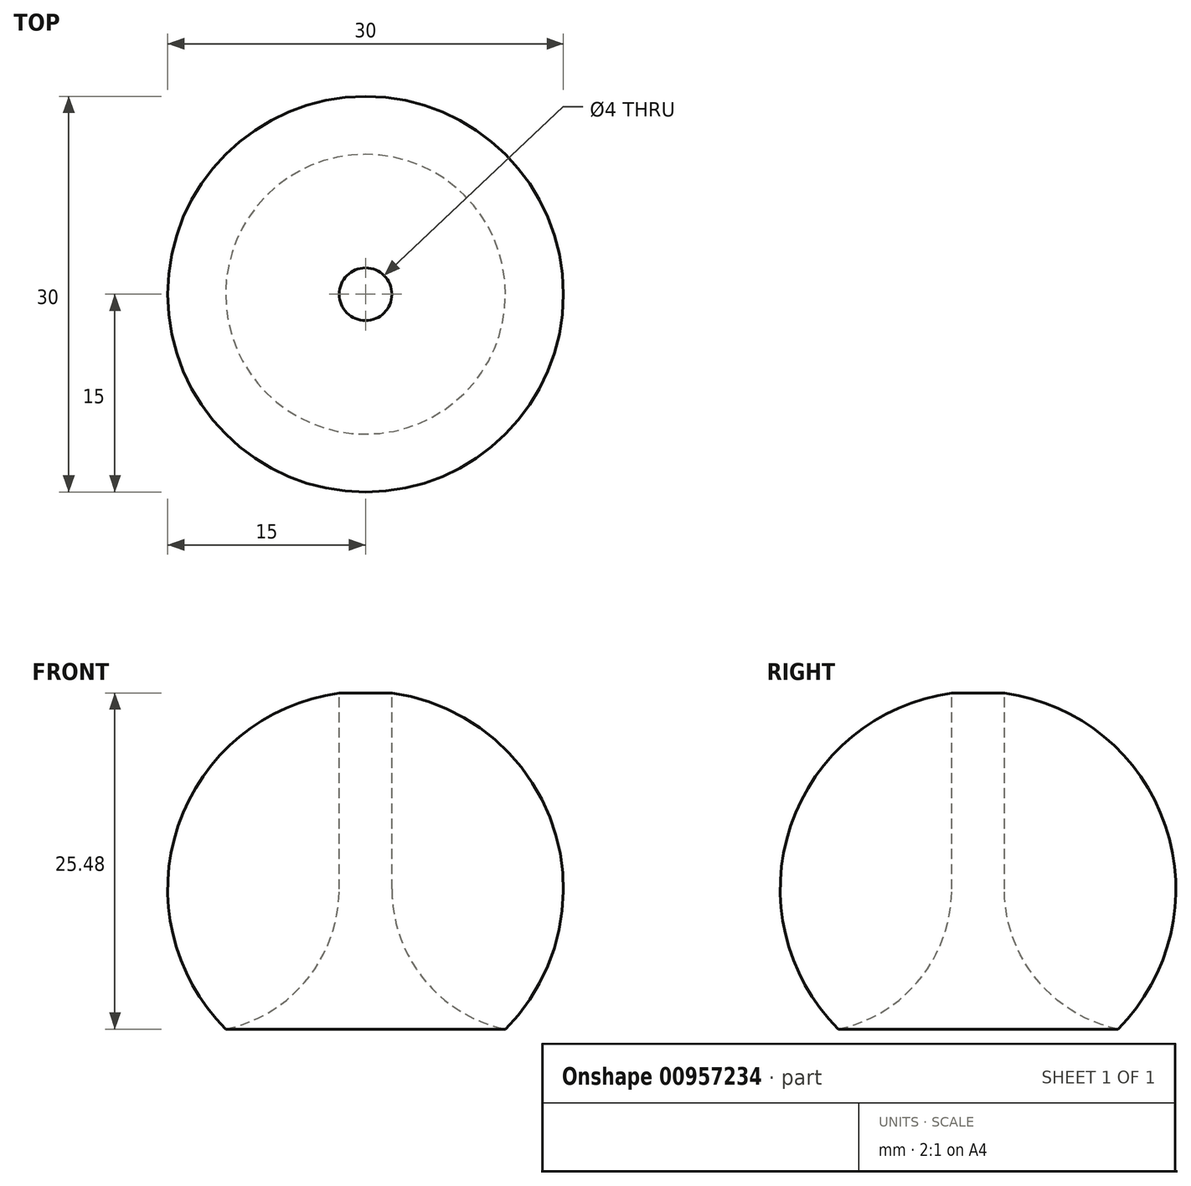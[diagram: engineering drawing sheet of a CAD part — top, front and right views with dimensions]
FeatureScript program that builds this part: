
annotation { "Feature Type Name" : "Feature", "Feature Type Description" : "" }
export const myFeature = defineFeature(function(context is Context, id is Id, definition is map)
    precondition{}
    {
        {
            var Q0;
            Q0=qCreatedBy(makeId("Right.planeOp"),FACE);
            var sketch = newSketch(context, id + "F0", { "sketchPlane" : qUnion([Q0])});
            skArc(sketch, "E0", {"start": v(0, -15) * mm, "mid": v(14.97, -1) * mm, "end": v(2, 14.87) * mm});
            skLineSegment(sketch, "E1.top", {"start": v(0, 19.21) * mm, "end": v(2, 19.21) * mm});
            skLineSegment(sketch, "E1.left", {"start": v(0, 0) * mm, "end": v(0, 19.21) * mm});
            skLineSegment(sketch, "E1.right", {"start": v(2, 14.87) * mm, "end": v(2, 19.21) * mm});
            skLineSegment(sketch, "E2", {"start": v(0, 0) * mm, "end": v(0, -15) * mm});
            skLineSegment(sketch, "E3", {"start": v(10.6, 10.6) * mm, "end": v(2, 19.21) * mm, "construction": true});
            skArc(sketch, "E4", {"start": v(2, 0) * mm, "mid": v(21.26, -6.83) * mm, "end": v(10.6, 10.6) * mm});
            skLineSegment(sketch, "E5", {"start": v(2, 0) * mm, "end": v(2, 14.87) * mm});
            skSolve(sketch);
        }
        {
            var Q0;
            Q0=makeQuery(id+"F0.imprint","IMPRINT",FACE,{"disambiguationData":[TD([[makeQuery(id+"F0.imprint","IMPRINT",EDGE,{"derivedFrom":sQuery(id+"F0.wireOp",EDGE,"E0")}),1.0]])]});
            var Q1;
            Q1=sQuery(id+"F0.wireOp",EDGE,"E2");
            revolve(context, id + "F1", {"surfaceOperationType" : NewSurfaceOperationType.NEW, "entities" : qUnion([Q0]), "axis" : qUnion([Q1]), "revolveType" : RevolveType.FULL});
        }
    });
